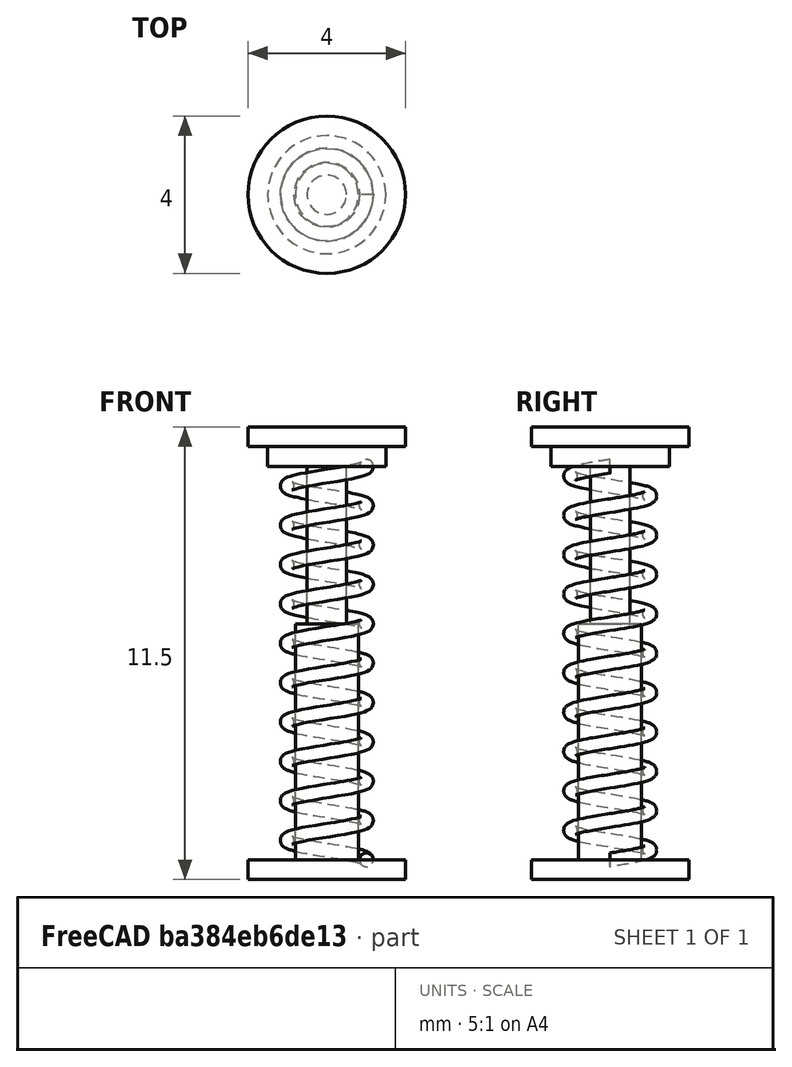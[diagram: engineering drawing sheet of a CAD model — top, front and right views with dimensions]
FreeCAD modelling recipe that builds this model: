
FCSTD DOCUMENT  (FreeCAD 0.18R16146 (Git))
Label: amortiguador
License: All rights reserved
LicenseURL: http://en.wikipedia.org/wiki/All_rights_reserved
objects: Part::Cylinder×5, Part::Helix×1, Sketcher::SketchObject×1, PartDesign::Body×1, Part::Sweep×1
note: 9 computed .brp shape members not serialized (recipe doc carries the construction recipe); baked Part::Feature solids carry a one-line shape summary decoded from their .brp

FEATURE [Part::Helix] Helix  label="Hélice"
  Angle = 0
  AttacherType = Attacher::AttachEngine3D
  Height = 10
  LocalCoord = 0
  Pitch = 1
  Radius = 1
  Style = 1
FEATURE [Sketcher::SketchObject] Sketch
  MapMode = 5
  Placement = pos=(0,0,0) rot=(1,0,0;1.5708rad)
  Support = -> [XZ_Plane]
  sketch-geometry (1):
    g0: Circle CenterX=1.00661 CenterY=0 CenterZ=0 NormalX=0 NormalY=0 NormalZ=1 AngleXU=0 Radius=0.175
  constraints (2):
    c: PointOnObject(g0,g-1)
    c: Diameter(g0) = 0.35
FEATURE [PartDesign::Body] Body
  Group = -> [Sketch]
  Origin = -> Origin
FEATURE [Part::Sweep] Sweep
  Frenet = true
  Sections = -> [Sketch]
  Solid = true
  Spine = -> Helix [Edge10,Edge9,Edge8,Edge7,Edge6,Edge5,Edge4,Edge3,Edge2,Edge1]
  Transition = 1
FEATURE [Part::Cylinder] Cylinder  label="Cilindro"
  Angle = 360
  AttacherType = Attacher::AttachEngine3D
  Height = 6
  Radius = 0.8
FEATURE [Part::Cylinder] Cylinder001  label="Cilindro001"
  Angle = 360
  AttacherType = Attacher::AttachEngine3D
  Height = 4
  Placement = pos=(0,0,6) rot=(0,0,1;0rad)
  Radius = 0.5
FEATURE [Part::Cylinder] Cylinder002  label="Cilindro002"
  Angle = 360
  AttacherType = Attacher::AttachEngine3D
  Height = 0.5
  Placement = pos=(0,0,10.5) rot=(0,0,1;0rad)
  Radius = 2
FEATURE [Part::Cylinder] Cylinder003  label="Cilindro003"
  Angle = 360
  AttacherType = Attacher::AttachEngine3D
  Height = 0.5
  Placement = pos=(0,0,10) rot=(0,0,1;0rad)
  Radius = 1.5
FEATURE [Part::Cylinder] Cylinder004  label="Cilindro004"
  Angle = 360
  AttacherType = Attacher::AttachEngine3D
  Height = 0.5
  Placement = pos=(0,0,-0.5) rot=(0,0,1;0rad)
  Radius = 2
